FCSTD DOCUMENT  (FreeCAD 0.21R33668 +26 (Git))
Label: animataion-rotate-engine-006
License: All rights reserved
LicenseURL: http://en.wikipedia.org/wiki/All_rights_reserved
objects: App::Link×6, PartDesign::CoordinateSystem×5, App::DocumentObjectGroup×3, Sketcher::SketchObject×2, App::FeaturePython×1, App::Part×1
note: 7 computed .brp shape members not serialized (recipe doc carries the construction recipe); baked Part::Feature solids carry a one-line shape summary decoded from their .brp
EXTERNAL_REF file=doigt_index_prothese.FCStd obj=LCS_005
EXTERNAL_REF file=doigt_index_prothese.FCStd obj=Body_2
EXTERNAL_REF file=doigt_index_prothese.FCStd obj=LCS_004
EXTERNAL_REF file=doigt_index_prothese.FCStd obj=tip_cover
EXTERNAL_REF file=doigt_index_prothese.FCStd obj=LCS_002
EXTERNAL_REF file=doigt_index_prothese.FCStd obj=middle_segment
EXTERNAL_REF file=doigt_index_prothese.FCStd obj=LCS_001
EXTERNAL_REF file=doigt_index_prothese.FCStd obj=middle_bumper
EXTERNAL_REF file=doigt_index_prothese.FCStd obj=LCS_0
EXTERNAL_REF file=doigt_index_prothese.FCStd obj=Body
EXTERNAL_REF file=doigt_index_prothese.FCStd obj=LCS_003
EXTERNAL_REF file=doigt_index_prothese.FCStd obj=index_socket

FEATURE [App::DocumentObjectGroup] Parts
FEATURE [App::DocumentObjectGroup] Constraints
FEATURE [App::FeaturePython] Variables  # WARN: FeaturePython — macro-defined, semantics opaque (R4)
  Angle_Rotation = 274
  Longueur_1 = 78
  Type = App::PropertyContainer
FEATURE [App::DocumentObjectGroup] Configurations
FEATURE [PartDesign::CoordinateSystem] LCS_Mobile  label="LCS_Engine"
  AttacherType = Attacher::AttachEngine3D
  AttachmentOffset = pos=(30,0,-19) rot=(0,0,1;0rad)
  MapMode = 2
  Placement = pos=(30,0,-19) rot=(0,0,1;0rad)
  Support = -> [X_Axis]
FEATURE [Sketcher::SketchObject] Barre  label="Sketch_Engine"
  AttachmentOffset = pos=(0,0,0) rot=(0,0,1;-4.7822rad)
  FullyConstrained = false
  MapMode = 3
  Placement = pos=(30,0,-19) rot=(0.604214,-0.563438,0.563438;2.05457rad)
  Support = -> [LCS_Mobile]
  expr: .AttachmentOffset.Rotation.Angle = -Variables.Angle_Rotation
  sketch-geometry (2):
    g0: Circle CenterX=0 CenterY=0 CenterZ=0 NormalX=0 NormalY=0 NormalZ=1 AngleXU=0 Radius=6
    g1: LineSegment StartX=0 StartY=0 StartZ=0 EndX=-6 EndY=0.000815193 EndZ=0
  constraints (4):
    c: Coincident(g0,g-1)
    c: Radius(g0) = 6
    c: Coincident(g1,g0)
    c: PointOnObject(g1,g0)
FEATURE [PartDesign::CoordinateSystem] LCS_Origin
  AttacherType = Attacher::AttachEngine3D
  MapMode = 2
  Support = -> [X_Axis]
FEATURE [Sketcher::SketchObject] Sketch_Leg  label="Sketch_Finger"
  ExternalGeometry = -> [Barre]
  FullyConstrained = true
  MapMode = 3
  Placement = pos=(0,0,0) rot=(1,0,0;1.5708rad)
  Support = -> [LCS_Origin]
  expr: Constraints[0] = Variables.Longueur_1 * 0.9
  expr: Constraints[1] = Variables.Longueur_1 * 0.35
  expr: Constraints[2] = Variables.Longueur_1 * 0.62
  expr: Constraints[3] = Variables.Longueur_1 * 0.24
  expr: Constraints[4] = Variables.Longueur_1 * 0.2308
  expr: Constraints[5] = Variables.Longueur_1 * 0.56
  expr: Constraints[6] = Variables.Longueur_1 * 0.43
  expr: Constraints[7] = Variables.Longueur_1 * 0.48
  expr: Constraints[8] = Variables.Longueur_1 * 0.22
  expr: Constraints[9] = Variables.Longueur_1 * 0.32
  sketch-geometry (10):
    g0: LineSegment StartX=0 StartY=0 StartZ=0 EndX=-7.7027 EndY=-47.7426 EndZ=0
    g1: LineSegment StartX=-7.7027 StartY=-47.7426 StartZ=0 EndX=-16.2529 EndY=21.9347 EndZ=0
    g2: LineSegment StartX=0 StartY=0 StartZ=0 EndX=-16.2529 EndY=21.9347 EndZ=0
    g3: LineSegment StartX=-7.7027 StartY=-47.7426 StartZ=0 EndX=29.5806 EndY=-24.9853 EndZ=0
    g4: LineSegment StartX=29.5806 StartY=-24.9853 StartZ=0 EndX=17.6114 EndY=6.34628 EndZ=0
    g5: LineSegment StartX=-16.2529 StartY=21.9347 StartZ=0 EndX=1.42351 EndY=25.345 EndZ=0
    g6: LineSegment StartX=17.6114 StartY=6.34628 StartZ=0 EndX=1.42351 EndY=25.345 EndZ=0
    g7: LineSegment StartX=17.6114 StartY=6.34628 StartZ=0 EndX=0 EndY=0 EndZ=0
    g8: LineSegment StartX=1.42351 StartY=25.345 StartZ=0 EndX=34.6772 EndY=8.14202 EndZ=0
    g9: LineSegment StartX=34.6772 StartY=8.14202 StartZ=0 EndX=17.6114 EndY=6.34628 EndZ=0
  constraints (25):
    c: Distance(g1) = 70.2
    c: Distance(g2) = 27.3
    c: Distance(g0) = 48.36
    c: Distance(g7) = 18.72
    c: Distance(g5) = 18.0024
    c: Distance(g3) = 43.68
    c: Distance(g4) = 33.54
    c: Distance(g8) = 37.44
    c: Distance(g9) = 17.16
    c: Distance(g6) = 24.96
    c: Coincident(g8,g9)
    c: Coincident(g8,g6)
    c: Coincident(g8,g5)
    c: Coincident(g7,g6)
    c: Coincident(g7,g9)
    c: Coincident(g7,g4)
    c: Coincident(g0,g-1)
    c: Coincident(g0,g2)
    c: Coincident(g0,g7)
    c: Coincident(g4,g3)
    c: Coincident(g1,g5)
    c: Coincident(g1,g2)
    c: Coincident(g0,g3)
    c: Coincident(g0,g1)
    c: Coincident(g3,g-3)
FEATURE [PartDesign::CoordinateSystem] LCS_Socket
  AttacherType = Attacher::AttachEngine3D
  MapMode = 7
  Placement = pos=(-7.7027,-1.06e-14,-47.7426) rot=(0.706447,0.706447,0.043183;3.05528rad)
  Support = -> [Sketch_Leg]
FEATURE [PartDesign::CoordinateSystem] LCS_LastSegment
  AttacherType = Attacher::AttachEngine3D
  MapMode = 7
  Placement = pos=(1.42351,5.6e-15,25.345) rot=(0.461258,-0.461258,-0.757946;1.84446rad)
  Support = -> [Sketch_Leg]
FEATURE [App::Link] tip_knuckle
  AttachedBy = #LCS_005
  AttachedTo = Parent Assembly#LCS_LastSegment
  AttachmentOffset = pos=(0,0,18) rot=(1,0,0;4.71239rad)
  LinkPlacement = pos=(-14.5639,8.6e-15,33.6157) rot=(0.230101,-0.230101,0.945572;4.65645rad)
  LinkedObject = -> <external doigt_index_prothese.FCStd>#Body_2
  Placement = pos=(-14.5639,8.6e-15,33.6157) rot=(0.230101,-0.230101,0.945572;4.65645rad)
  SolverId = Asm4EE
  expr: Placement = LCS_LastSegment.Placement * AttachmentOffset * doigt_index_prothese#LCS_005.Placement ^ -1
FEATURE [App::Link] tip_cover
  AttachedBy = #LCS_004
  AttachedTo = Parent Assembly#LCS_LastSegment
  AttachmentOffset = pos=(0,0,-6) rot=(1,0,0;3.14159rad)
  LinkPlacement = pos=(6.75263,4.6e-15,22.5881) rot=(0.649522,-0.649522,0.395275;3.89445rad)
  LinkedObject = -> <external doigt_index_prothese.FCStd>#tip_cover
  Placement = pos=(6.75263,4.6e-15,22.5881) rot=(0.649522,-0.649522,0.395275;3.89445rad)
  SolverId = Asm4EE
  expr: Placement = LCS_LastSegment.Placement * AttachmentOffset * doigt_index_prothese#LCS_004.Placement ^ -1
FEATURE [PartDesign::CoordinateSystem] LCS_MiddleSegment
  AttacherType = Attacher::AttachEngine3D
  MapMode = 7
  Placement = pos=(-16.2529,4.9e-15,21.9347) rot=(0.61068,-0.61068,-0.504123;2.20771rad)
  Support = -> [Sketch_Leg]
FEATURE [App::Link] middle_segment
  AttachedBy = #LCS_002
  AttachedTo = Parent Assembly#LCS_MiddleSegment
  AttachmentOffset = pos=(0,0,0) rot=(0.707107,0,0.707107;3.14159rad)
  LinkPlacement = pos=(-16.2529,4.9e-15,21.9347) rot=(-0.067434,-0.705497,0.705497;3.27626rad)
  LinkedObject = -> <external doigt_index_prothese.FCStd>#middle_segment
  Placement = pos=(-16.2529,4.9e-15,21.9347) rot=(-0.067434,-0.705497,0.705497;3.27626rad)
  SolverId = Asm4EE
  expr: Placement = LCS_MiddleSegment.Placement * AttachmentOffset * doigt_index_prothese#LCS_002.Placement ^ -1
FEATURE [App::Link] middle_bumper
  AttachedBy = #LCS_001
  AttachedTo = Parent Assembly#LCS_MiddleSegment
  AttachmentOffset = pos=(0,0,-9) rot=(1,0,0;3.14159rad)
  LinkPlacement = pos=(-7.41589,4.9e-15,23.6397) rot=(0.537028,-0.537028,0.65054;4.2951rad)
  LinkedObject = -> <external doigt_index_prothese.FCStd>#middle_bumper
  Placement = pos=(-7.41589,4.9e-15,23.6397) rot=(0.537028,-0.537028,0.65054;4.2951rad)
  SolverId = Asm4EE
  expr: Placement = LCS_MiddleSegment.Placement * AttachmentOffset * doigt_index_prothese#LCS_001.Placement ^ -1
FEATURE [App::Link] finger_base_knuckle001  label="finger_base_knuckle"
  AttachedBy = #LCS_0
  AttachedTo = Parent Assembly#LCS_Socket
  AttachmentOffset = pos=(0,0,-70) rot=(0,1,0;3.14159rad)
  LinkPlacement = pos=(-16.2286,4.9e-15,21.7362) rot=(-0.060899,0.060899,0.996284;4.70867rad)
  LinkedObject = -> <external doigt_index_prothese.FCStd>#Body
  Placement = pos=(-16.2286,4.9e-15,21.7362) rot=(-0.060899,0.060899,0.996284;4.70867rad)
  SolverId = Asm4EE
  expr: Placement = LCS_Socket.Placement * AttachmentOffset * doigt_index_prothese#LCS_0.Placement ^ -1
FEATURE [App::Link] index_socket001  label="index_socket"
  AttachedBy = #LCS_003
  AttachedTo = Parent Assembly#LCS_Socket
  AttachmentOffset = pos=(0,0,-64) rot=(0,0,1;0rad)
  LinkPlacement = pos=(-15.4978,3.6e-15,15.7809) rot=(0.706447,0.706447,0.043183;3.05528rad)
  LinkedObject = -> <external doigt_index_prothese.FCStd>#index_socket
  Placement = pos=(-15.4978,3.6e-15,15.7809) rot=(0.706447,0.706447,0.043183;3.05528rad)
  SolverId = Asm4EE
  expr: Placement = LCS_Socket.Placement * AttachmentOffset * doigt_index_prothese#LCS_003.Placement ^ -1
FEATURE [App::Part] Assembly
  AssemblyType = Part::Link
  Group = -> [Constraints,Variables,Configurations,Barre,LCS_Mobile,Sketch_Leg,LCS_Origin,LCS_Socket,LCS_LastSegment,tip_knuckle,tip_cover,LCS_MiddleSegment,middle_segment,middle_bumper,finger_base_knuckle001,index_socket001]
  Origin = -> Origin
  Type = Assembly

RESOLVED EXTERNAL PARTS (link-assembly join: the EXTERNAL_REF files above that resolve inside this repo's crawl, each included once):
---- part doigt_index_prothese.FCStd = doc fcstd_df8f533a6901 ----
FCSTD DOCUMENT  (FreeCAD 0.21R33668 +26 (Git))
Label: doigt_index_prothese
License: All rights reserved
LicenseURL: http://en.wikipedia.org/wiki/All_rights_reserved
objects: Part::Feature×7, PartDesign::CoordinateSystem×6, PartDesign::FeatureBase×6, PartDesign::Body×6, Part::FeaturePython×1, App::AnnotationLabel×1, App::DocumentObjectGroup×1
note: 26 computed .brp shape members not serialized (recipe doc carries the construction recipe); baked Part::Feature solids carry a one-line shape summary decoded from their .brp

FEATURE [PartDesign::CoordinateSystem] LCS_0
  AttacherType = Attacher::AttachEngine3D
  MapMode = 2
  Support = -> [X_Axis]
FEATURE [Part::Feature] finger_base_knuckle_v3_5_006_solid  label="finger_base_knuckle_v3_5_006 (Solid)"
  shape: bbox 18.5 x 17.25 x 15.15 mm, 17542 faces (baked)
FEATURE [PartDesign::FeatureBase] BaseFeature
  BaseFeature = -> finger_base_knuckle_v3_5_006_solid
FEATURE [PartDesign::Body] Body  label="finger_base_knuckle"
  BaseFeature = -> finger_base_knuckle_v3_5_006_solid
  Group = -> [BaseFeature,LCS_0]
  Origin = -> Origin
  Placement = pos=(0,0,6) rot=(0,0,1;0rad)
  Tip = -> BaseFeature
FEATURE [PartDesign::CoordinateSystem] LCS_001
  AttacherType = Attacher::AttachEngine3D
  MapMode = 2
  Support = -> [X_Axis001]
FEATURE [Part::Feature] dangercreations_finger_v3_5_5_index_middle_bumper001_solid  label="dangercreations_finger_v3_5_5_index_middle_bumper001 (Solid)"
  shape: bbox 11.89 x 15.5 x 6 mm, 3652 faces (baked)
FEATURE [PartDesign::FeatureBase] BaseFeature001
  BaseFeature = -> dangercreations_finger_v3_5_5_index_middle_bumper001_solid
FEATURE [PartDesign::Body] middle_bumper
  BaseFeature = -> dangercreations_finger_v3_5_5_index_middle_bumper001_solid
  Group = -> [BaseFeature001,LCS_001]
  Origin = -> Origin001
  Placement = pos=(0,0,20) rot=(0,0,1;0rad)
  Tip = -> BaseFeature001
FEATURE [PartDesign::CoordinateSystem] LCS_002
  AttacherType = Attacher::AttachEngine3D
  MapMode = 2
  Support = -> [X_Axis002]
FEATURE [Part::Feature] dangercreations_finger_v3_5_5_index_middle_segment001_solid  label="dangercreations_finger_v3_5_5_index_middle_segment001 (Solid)"
  shape: bbox 28 x 12.5 x 8.52 mm, 17486 faces (baked)
FEATURE [PartDesign::FeatureBase] BaseFeature002
  BaseFeature = -> dangercreations_finger_v3_5_5_index_middle_segment001_solid
FEATURE [PartDesign::Body] middle_segment
  BaseFeature = -> dangercreations_finger_v3_5_5_index_middle_segment001_solid
  Group = -> [BaseFeature002,LCS_002]
  Origin = -> Origin002
  Placement = pos=(-3e-15,0,34) rot=(0,1,0;1.5708rad)
  Tip = -> BaseFeature002
FEATURE [Part::Feature] dangercreations_finger_v3_5_5_index_finger_socket001_solid  label="dangercreations_finger_v3_5_5_index_finger_socket001 (Solid)"
  shape: bbox 23.06 x 23.04 x 71 mm, 6810 faces (baked)
FEATURE [PartDesign::CoordinateSystem] LCS_003
  AttacherType = Attacher::AttachEngine3D
  MapMode = 2
  Support = -> [X_Axis003]
FEATURE [Part::Feature] dangercreations_finger_v3_5_5_index_finger_socket001_solid001  label="dangercreations_finger_v3_5_5_index_finger_socket001 (Solid)001"
  shape: bbox 23.06 x 23.04 x 71 mm, 6810 faces (baked)
FEATURE [PartDesign::FeatureBase] BaseFeature003
  BaseFeature = -> dangercreations_finger_v3_5_5_index_finger_socket001_solid001
FEATURE [PartDesign::Body] index_socket
  BaseFeature = -> dangercreations_finger_v3_5_5_index_finger_socket001_solid001
  Group = -> [BaseFeature003,LCS_003]
  Origin = -> Origin003
  Placement = pos=(0,9e-15,-14) rot=(0,1,0;3.14159rad)
  Tip = -> BaseFeature003
FEATURE [PartDesign::CoordinateSystem] LCS_004
  AttacherType = Attacher::AttachEngine3D
  MapMode = 2
  Support = -> [X_Axis004]
FEATURE [Part::Feature] dangercreations_finger_v3_5_5_index_tip_cover001_solid  label="dangercreations_finger_v3_5_5_index_tip_cover001 (Solid)"
  Placement = pos=(0,0,102) rot=(0,0,1;0rad)
  shape: bbox 13.5 x 13.08 x 20.4 mm, 6572 faces (baked)
FEATURE [PartDesign::FeatureBase] BaseFeature004
  BaseFeature = -> dangercreations_finger_v3_5_5_index_tip_cover001_solid
FEATURE [PartDesign::Body] tip_cover
  BaseFeature = -> dangercreations_finger_v3_5_5_index_tip_cover001_solid
  Group = -> [BaseFeature004,LCS_004]
  Origin = -> Origin004
  Placement = pos=(0,0,84) rot=(0,0,1;0rad)
  Tip = -> BaseFeature004
FEATURE [PartDesign::CoordinateSystem] LCS_005
  AttacherType = Attacher::AttachEngine3D
  MapMode = 2
  Support = -> [X_Axis005]
FEATURE [Part::Feature] dangercreations_finger_v3_5_5_index_tip_knuckle001_solid  label="dangercreations_finger_v3_5_5_index_tip_knuckle001 (Solid)"
  shape: bbox 15.5 x 18.5 x 13 mm, 13648 faces (baked)
FEATURE [PartDesign::FeatureBase] BaseFeature005
  BaseFeature = -> dangercreations_finger_v3_5_5_index_tip_knuckle001_solid
FEATURE [PartDesign::Body] Body_2  label="tip_knuckle"
  BaseFeature = -> dangercreations_finger_v3_5_5_index_tip_knuckle001_solid
  Group = -> [BaseFeature005,LCS_005]
  Origin = -> Origin005
  Placement = pos=(0,-1e-14,47) rot=(1,0,0;1.5708rad)
  Tip = -> BaseFeature005
FEATURE [Part::FeaturePython] DistPoints  # WARN: FeaturePython — macro-defined, semantics opaque (R4)
FEATURE [App::AnnotationLabel] MeasureLbl
  BasePosition = (-4.25,-0.0706348,41.9223)
  LabelText = D = 18,00 mm
  TextPosition = (0,0,0)
FEATURE [App::DocumentObjectGroup] Measures
  Group = -> [DistPoints,MeasureLbl]
